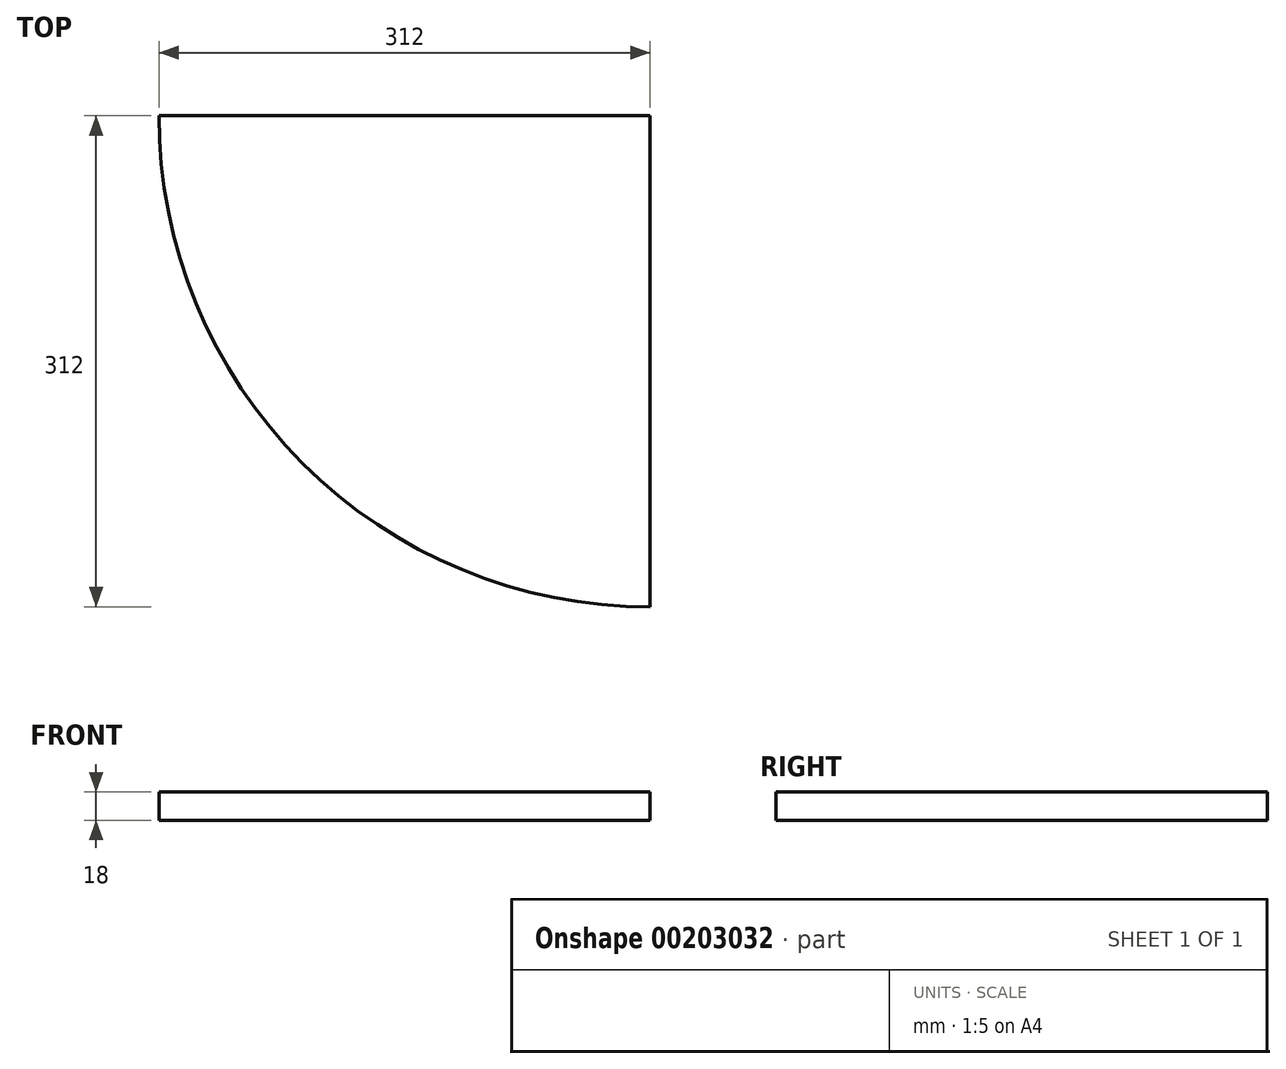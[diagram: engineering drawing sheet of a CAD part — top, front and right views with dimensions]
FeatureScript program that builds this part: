
annotation { "Feature Type Name" : "Feature", "Feature Type Description" : "" }
export const myFeature = defineFeature(function(context is Context, id is Id, definition is map)
    precondition{}
    {
        {
            var Q0;
            Q0=qCreatedBy(makeId("Top.planeOp"),FACE);
            var sketch = newSketch(context, id + "F0", { "sketchPlane" : qUnion([Q0])});
            skLineSegment(sketch, "E0", {"start": v(0, 0) * mm, "end": v(0, 312) * mm});
            skLineSegment(sketch, "E1", {"start": v(0, 312) * mm, "end": v(-312, 312) * mm});
            skArc(sketch, "E2", {"start": v(-312, 312) * mm, "mid": v(-220.77, 91.23) * mm, "end": v(0, 0) * mm});
            skSolve(sketch);
        }
        {
            var Q0;
            Q0 = qSketchRegion(id + "F0", true);
            extrude(context, id + "F1", {"entities" : qUnion([Q0]), "depth" : 18 * mm});
        }
    });
